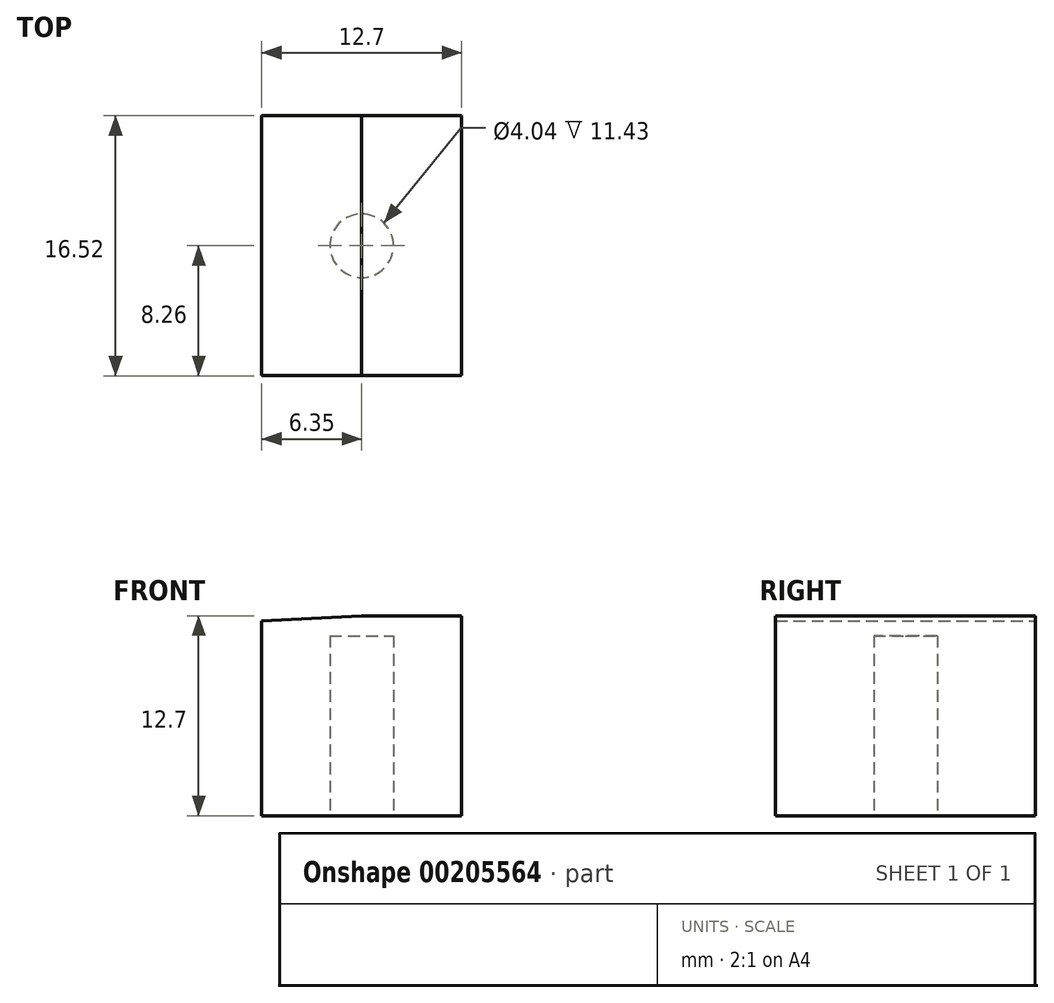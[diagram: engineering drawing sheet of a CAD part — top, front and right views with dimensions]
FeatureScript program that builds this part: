
annotation { "Feature Type Name" : "Feature", "Feature Type Description" : "" }
export const myFeature = defineFeature(function(context is Context, id is Id, definition is map)
    precondition{}
    {
        {
            var Q0;
            Q0=qCreatedBy(makeId("Front.planeOp"),FACE);
            var sketch = newSketch(context, id + "F0", { "sketchPlane" : qUnion([Q0])});
            skLineSegment(sketch, "E0", {"start": v(0, 0) * mm, "end": v(0, 12.7) * mm});
            skLineSegment(sketch, "E1", {"start": v(0, 12.7) * mm, "end": v(-6.35, 12.7) * mm});
            skLineSegment(sketch, "E2", {"start": v(-6.35, 12.7) * mm, "end": v(-12.7, 12.37) * mm});
            skLineSegment(sketch, "E3", {"start": v(-12.7, 12.37) * mm, "end": v(-12.7, 0) * mm});
            skLineSegment(sketch, "E4", {"start": v(-12.7, 0) * mm, "end": v(0, 0) * mm});
            skSolve(sketch);
        }
        {
            var Q0;
            Q0=qSketchRegion(id+"F0",true);
            extrude(context, id + "F1", {"entities" : qUnion([Q0]), "depth" : 16.5 * mm, "symmetric" : true});
        }
        {
            var Q0;
            Q0=makeQuery(id+"F1.opExtrude","SWEPT_FACE",FACE,{"disambiguationData":[OSD([sQuery(id+"F0.wireOp",EDGE,"E4")])]});
            var sketch = newSketch(context, id + "F2", { "sketchPlane" : qUnion([Q0])});
            skCircle(sketch, "E5", {"center": v(-6.35, 0) * mm, "radius": 2.02 * mm});
            skSolve(sketch);
        }
        {
            var Q0;
            Q0=qSketchRegion(id+"F2",true);
            extrude(context, id + "F3", {"entities" : qUnion([Q0]), "operationType" : NewBodyOperationType.REMOVE, "oppositeDirection" : true, "depth" : 11.43 * mm});
        }
    });
